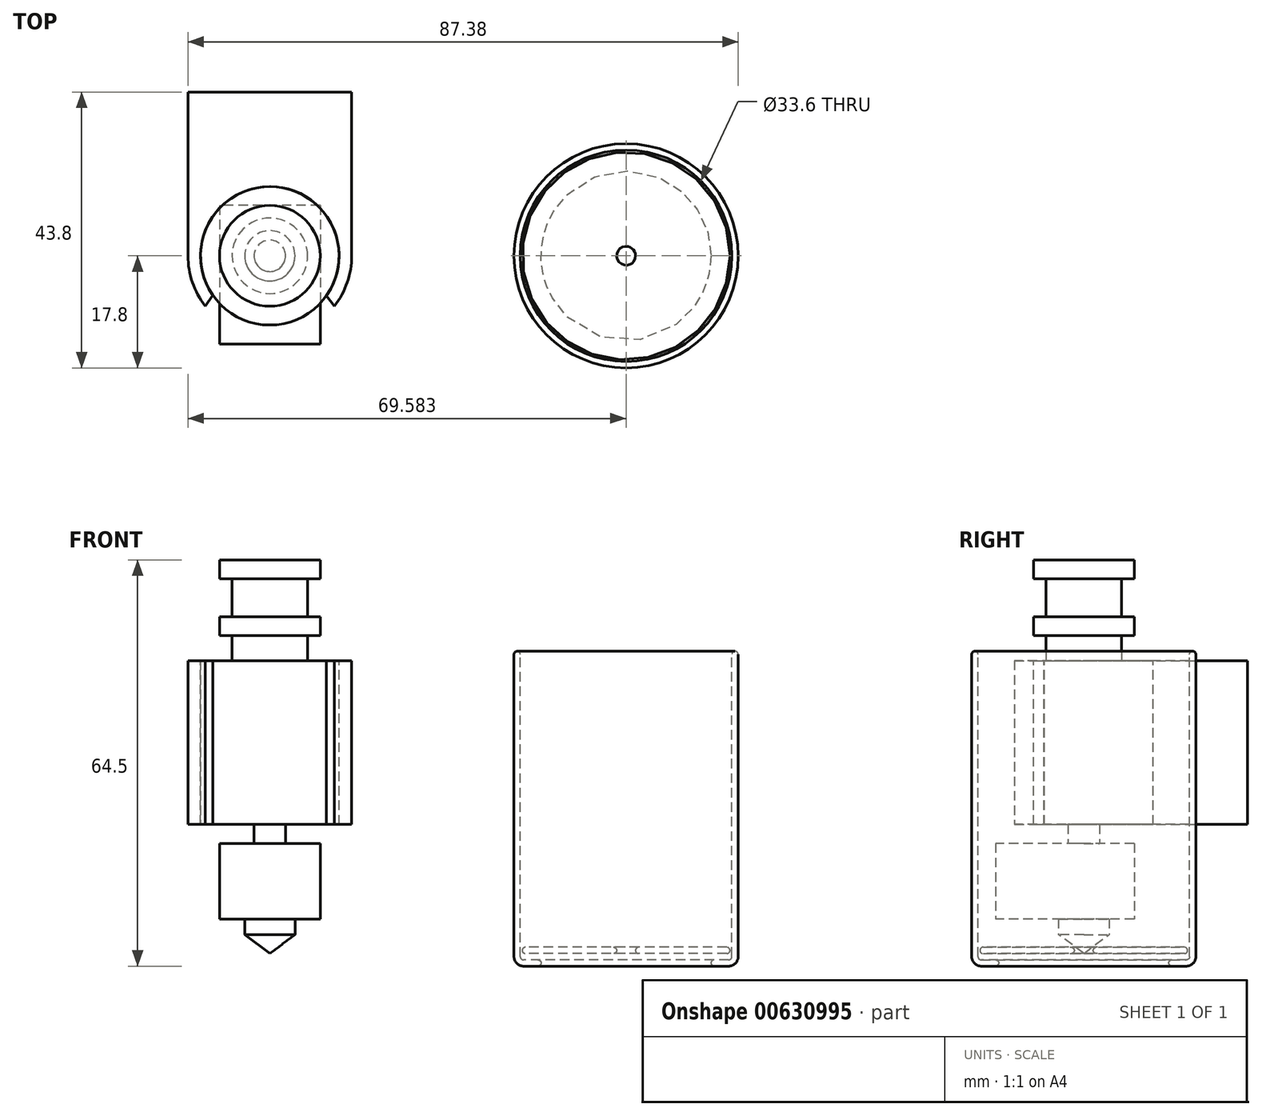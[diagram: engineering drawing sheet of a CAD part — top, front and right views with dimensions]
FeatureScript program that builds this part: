
annotation { "Feature Type Name" : "Feature", "Feature Type Description" : "" }
export const myFeature = defineFeature(function(context is Context, id is Id, definition is map)
    precondition{}
    {
        {
            var Q0;
            Q0=qCreatedBy(makeId("Front.planeOp"),FACE);
            var sketch = newSketch(context, id + "F0", { "sketchPlane" : qUnion([Q0])});
            skLineSegment(sketch, "E0", {"start": v(0, 62.5) * mm, "end": v(8, 62.5) * mm});
            skLineSegment(sketch, "E1", {"start": v(8, 62.5) * mm, "end": v(8, 59.5) * mm});
            skLineSegment(sketch, "E2", {"start": v(8, 59.5) * mm, "end": v(6, 59.5) * mm});
            skLineSegment(sketch, "E3", {"start": v(6, 59.5) * mm, "end": v(6, 53.5) * mm});
            skLineSegment(sketch, "E4", {"start": v(6, 53.5) * mm, "end": v(8, 53.5) * mm});
            skLineSegment(sketch, "E5", {"start": v(8, 53.5) * mm, "end": v(8, 50.5) * mm});
            skLineSegment(sketch, "E6", {"start": v(8, 50.5) * mm, "end": v(6, 50.5) * mm});
            skLineSegment(sketch, "E7", {"start": v(6, 50.5) * mm, "end": v(6, 46.5) * mm});
            skLineSegment(sketch, "E8", {"start": v(6, 46.5) * mm, "end": v(11, 46.5) * mm});
            skLineSegment(sketch, "E9", {"start": v(11, 46.5) * mm, "end": v(11, 20.5) * mm});
            skLineSegment(sketch, "E10", {"start": v(11, 20.5) * mm, "end": v(2.5, 20.5) * mm});
            skLineSegment(sketch, "E11", {"start": v(2.5, 20.5) * mm, "end": v(2.5, 5.5) * mm});
            skLineSegment(sketch, "E12", {"start": v(2.5, 5.5) * mm, "end": v(4, 5.5) * mm});
            skLineSegment(sketch, "E13", {"start": v(4, 5.5) * mm, "end": v(4, 3) * mm});
            skLineSegment(sketch, "E14", {"start": v(4, 3) * mm, "end": v(0, 0) * mm});
            skLineSegment(sketch, "E15", {"start": v(0, 0) * mm, "end": v(0, 62.5) * mm});
            skSolve(sketch);
        }
        {
            var Q0;
            Q0 = qSketchRegion(id + "F0", true);
            var Q1;
            Q1=sQuery(id+"F0.wireOp",EDGE,"E15");
            revolve(context, id + "F1", {"entities" : qUnion([Q0]), "axis" : qUnion([Q1]), "revolveType" : RevolveType.FULL});
        }
        {
            var Q0;
            Q0=makeQuery(id+"F1.opRevolve","SWEPT_FACE",FACE,{"disambiguationData":[OSD([sQuery(id+"F0.wireOp",EDGE,"E12")])]});
            var sketch = newSketch(context, id + "F2", { "sketchPlane" : qUnion([Q0])});
            skLineSegment(sketch, "E16.bottom", {"start": v(8, 8) * mm, "end": v(-8, 8) * mm});
            skLineSegment(sketch, "E16.top", {"start": v(8, -14) * mm, "end": v(-8, -14) * mm});
            skLineSegment(sketch, "E16.left", {"start": v(8, 8) * mm, "end": v(8, -14) * mm});
            skLineSegment(sketch, "E16.right", {"start": v(-8, 8) * mm, "end": v(-8, -14) * mm});
            skPoint(sketch, "E16.middle", {"position": v(0, -3) * mm});
            skSolve(sketch);
        }
        {
            var Q0;
            Q0=makeQuery(id+"F2.imprint","IMPRINT",FACE,{"disambiguationData":[TD([[makeQuery(id+"F2.imprint","IMPRINT",EDGE,{"derivedFrom":sQuery(id+"F2.wireOp",EDGE,"E16.bottom")}),1.0]])]});
            var Q1;
            {var subQ0=sQuery(id+"F0.wireOp",EDGE,"E12");Q1=makeQuery(id+"F2.imprint","IMPRINT",FACE,{"disambiguationData":[TD([[makeQuery(id+"F2.imprint","IMPRINT",EDGE,{"derivedFrom":makeQuery(id+"F1.opRevolve","SWEPT_EDGE",EDGE,{"disambiguationData":[OSD([sQuery(id+"F0.wireOp",EDGE,"E11"),subQ0])]})}),1.0]])]});}
            var Q2;
            Q2=makeQuery(id+"F2.imprint","IMPRINT",FACE,{"disambiguationData":[TD([[makeQuery(id+"F2.imprint","IMPRINT",EDGE,{"derivedFrom":makeQuery(id+"F1.opRevolve","SWEPT_EDGE",EDGE,{"disambiguationData":[OSD([sQuery(id+"F0.wireOp",EDGE,"E11"),sQuery(id+"F0.wireOp",EDGE,"E12")])]})}),-1.0]])]});
            extrude(context, id + "F3", {"entities" : qUnion([Q0, Q1, Q2]), "operationType" : NewBodyOperationType.ADD, "depth" : 12 * mm, "offsetDistance" : 25 * mm});
        }
        {
            var Q0;
            Q0=makeQuery(id+"F1.opRevolve","SWEPT_FACE",FACE,{"disambiguationData":[OSD([sQuery(id+"F0.wireOp",EDGE,"E8")])]});
            var sketch = newSketch(context, id + "F4", { "sketchPlane" : qUnion([Q0])});
            skArc(sketch, "E17", {"start": v(10.27, -7.97) * mm, "mid": v(12.3, -4.21) * mm, "end": v(13, 0) * mm});
            skArc(sketch, "E18", {"start": v(-10.27, -7.97) * mm, "mid": v(-12.3, -4.21) * mm, "end": v(-13, 0) * mm});
            skLineSegment(sketch, "E19", {"start": v(13, 0) * mm, "end": v(13, 26) * mm});
            skLineSegment(sketch, "E20", {"start": v(13, 26) * mm, "end": v(-13, 26) * mm});
            skLineSegment(sketch, "E21", {"start": v(-13, 26) * mm, "end": v(-13, 0) * mm});
            skLineSegment(sketch, "E22", {"start": v(10.27, -7.97) * mm, "end": v(8.98, -6.35) * mm});
            skLineSegment(sketch, "E23", {"start": v(-10.27, -7.97) * mm, "end": v(-9.05, -6.25) * mm});
            skSolve(sketch);
        }
        {
            var Q0;
            Q0=makeQuery(id+"F4.imprint","IMPRINT",FACE,{"disambiguationData":[TD([[makeQuery(id+"F4.imprint","IMPRINT",EDGE,{"derivedFrom":sQuery(id+"F4.wireOp",EDGE,"E17")}),1.0]])]});
            extrude(context, id + "F5", {"entities" : qUnion([Q0]), "oppositeDirection" : true, "depth" : 26 * mm, "offsetDistance" : 25 * mm});
        }
        {
            var Q0;
            Q0=qCreatedBy(makeId("Front.planeOp"),FACE);
            var sketch = newSketch(context, id + "F6", { "sketchPlane" : qUnion([Q0])});
            skLineSegment(sketch, "E24", {"start": v(56.58, 48.32) * mm, "end": v(56.58, -19.66) * mm, "construction": true});
            skLineSegment(sketch, "E25.bottom", {"start": v(58.08, 0) * mm, "end": v(73.08, 0) * mm});
            skLineSegment(sketch, "E25.top", {"start": v(58.08, 1) * mm, "end": v(73.08, 1) * mm});
            skLineSegment(sketch, "E25.left", {"start": v(58.08, 0) * mm, "end": v(58.08, 1) * mm});
            skLineSegment(sketch, "E25.right", {"start": v(73.08, 0) * mm, "end": v(73.08, 1) * mm});
            skLineSegment(sketch, "E26", {"start": v(70.08, -1) * mm, "end": v(73.38, -1) * mm});
            skLineSegment(sketch, "E27", {"start": v(73.38, -1) * mm, "end": v(73.38, 48) * mm});
            skLineSegment(sketch, "E28", {"start": v(73.38, 48) * mm, "end": v(74.38, 48) * mm});
            skLineSegment(sketch, "E29", {"start": v(74.38, 48) * mm, "end": v(74.38, -2) * mm});
            skLineSegment(sketch, "E30", {"start": v(74.38, -2) * mm, "end": v(70.08, -2) * mm});
            skLineSegment(sketch, "E31", {"start": v(70.08, -2) * mm, "end": v(70.08, -1) * mm});
            skSolve(sketch);
        }
        {
            var Q0;
            Q0=makeQuery(id+"F6.imprint","IMPRINT",FACE,{"disambiguationData":[TD([[makeQuery(id+"F6.imprint","IMPRINT",EDGE,{"derivedFrom":sQuery(id+"F6.wireOp",EDGE,"E26")}),-1.0]])]});
            var Q1;
            Q1=makeQuery(id+"F6.imprint","IMPRINT",FACE,{"disambiguationData":[TD([[makeQuery(id+"F6.imprint","IMPRINT",EDGE,{"derivedFrom":sQuery(id+"F6.wireOp",EDGE,"E25.bottom")}),1.0]])]});
            var Q2;
            Q2=sQuery(id+"F6.wireOp",EDGE,"E24");
            revolve(context, id + "F7", {"surfaceOperationType" : NewSurfaceOperationType.NEW, "entities" : qUnion([Q0, Q1]), "axis" : qUnion([Q2]), "revolveType" : RevolveType.FULL});
        }
        {
            var Q0;
            Q0=makeQuery(id+"F7.opRevolve","SWEPT_EDGE",EDGE,{"disambiguationData":[OSD([sQuery(id+"F6.wireOp",EDGE,"E29"),sQuery(id+"F6.wireOp",EDGE,"E30")])]});
            fillet(context, id + "F8", {"entities" : qUnion([Q0]), "tangentPropagation" : true, "radius" : 1.5 * mm, "defaultsChanged" : false, "vertexSettings" : [], "allowEdgeOverflow" : false});
        }
        {
            var Q0;
            Q0=makeQuery(id+"F7.opRevolve","SWEPT_EDGE",EDGE,{"disambiguationData":[OSD([sQuery(id+"F6.wireOp",EDGE,"E26"),sQuery(id+"F6.wireOp",EDGE,"E27")])]});
            var Q1;
            Q1=makeQuery(id+"F7.opRevolve","SWEPT_EDGE",EDGE,{"disambiguationData":[OSD([sQuery(id+"F6.wireOp",EDGE,"E26"),sQuery(id+"F6.wireOp",EDGE,"E31")])]});
            var Q2;
            Q2=makeQuery(id+"F7.opRevolve","SWEPT_EDGE",EDGE,{"disambiguationData":[OSD([sQuery(id+"F6.wireOp",EDGE,"E30"),sQuery(id+"F6.wireOp",EDGE,"E31")])]});
            var Q3;
            Q3=makeQuery(id+"F7.opRevolve","SWEPT_FACE",FACE,{"disambiguationData":[OSD([sQuery(id+"F6.wireOp",EDGE,"E25.top")])]});
            var Q4;
            Q4=makeQuery(id+"F7.opRevolve","SWEPT_EDGE",EDGE,{"disambiguationData":[OSD([sQuery(id+"F6.wireOp",EDGE,"E25.bottom"),sQuery(id+"F6.wireOp",EDGE,"E25.right")])]});
            var Q5;
            Q5=makeQuery(id+"F7.opRevolve","SWEPT_EDGE",EDGE,{"disambiguationData":[OSD([sQuery(id+"F6.wireOp",EDGE,"E28"),sQuery(id+"F6.wireOp",EDGE,"E29")])]});
            var Q6;
            Q6=makeQuery(id+"F7.opRevolve","SWEPT_FACE",FACE,{"disambiguationData":[OSD([sQuery(id+"F6.wireOp",EDGE,"E28")])]});
            var Q7;
            Q7=makeQuery(id+"F7.opRevolve","SWEPT_EDGE",EDGE,{"disambiguationData":[OSD([sQuery(id+"F6.wireOp",EDGE,"E25.bottom"),sQuery(id+"F6.wireOp",EDGE,"E25.left")])]});
            fillet(context, id + "F9", {"entities" : qUnion([Q0, Q1, Q2, Q3, Q4, Q5, Q6, Q7]), "tangentPropagation" : true, "radius" : 0.5 * mm, "defaultsChanged" : false, "vertexSettings" : [], "allowEdgeOverflow" : false});
        }
    });
